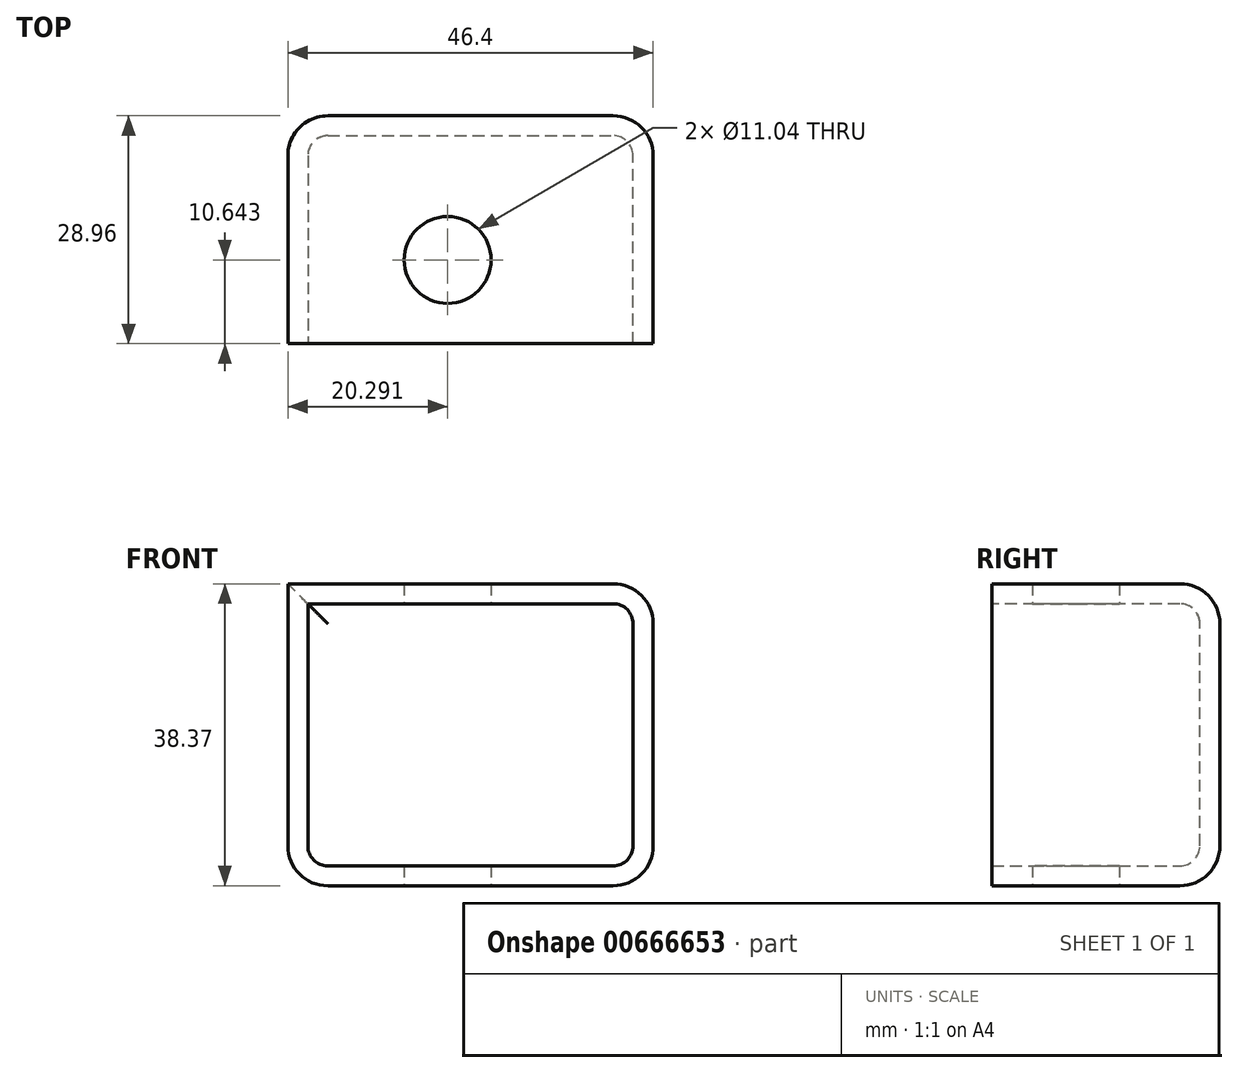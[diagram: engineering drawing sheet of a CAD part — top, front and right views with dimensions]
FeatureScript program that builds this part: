
annotation { "Feature Type Name" : "Feature", "Feature Type Description" : "" }
export const myFeature = defineFeature(function(context is Context, id is Id, definition is map)
    precondition{}
    {
        {
            var Q0;
            Q0=qCreatedBy(makeId("Front.planeOp"),FACE);
            var sketch = newSketch(context, id + "F0", { "sketchPlane" : qUnion([Q0])});
            skLineSegment(sketch, "E0.bottom", {"start": v(2.62, 0) * mm, "end": v(49.02, 0) * mm});
            skLineSegment(sketch, "E0.top", {"start": v(2.62, 38.37) * mm, "end": v(49.02, 38.37) * mm});
            skLineSegment(sketch, "E0.left", {"start": v(2.62, 0) * mm, "end": v(2.62, 38.37) * mm});
            skLineSegment(sketch, "E0.right", {"start": v(49.02, 0) * mm, "end": v(49.02, 38.37) * mm});
            skSolve(sketch);
        }
        {
            var Q0;
            Q0 = qSketchRegion(id + "F0", true);
            extrude(context, id + "F1", {"entities" : qUnion([Q0]), "endBound" : BoundingType.SYMMETRIC, "oppositeDirection" : true, "depth" : 28.96 * mm, "offsetDistance" : 25.4 * mm});
        }
        {
            var Q0;
            Q0=makeQuery(id+"F1.opExtrude","CAP_EDGE",EDGE,{"disambiguationData":[OSD([sQuery(id+"F0.wireOp",EDGE,"E0.right")])],"isStart":false});
            var Q1;
            Q1=makeQuery(id+"F1.opExtrude","SWEPT_EDGE",EDGE,{"disambiguationData":[OSD([sQuery(id+"F0.wireOp",EDGE,"E0.bottom"),sQuery(id+"F0.wireOp",EDGE,"E0.right")])]});
            var Q2;
            Q2=makeQuery(id+"F1.opExtrude","SWEPT_EDGE",EDGE,{"disambiguationData":[OSD([sQuery(id+"F0.wireOp",EDGE,"E0.bottom"),sQuery(id+"F0.wireOp",EDGE,"E0.left")])]});
            var Q3;
            Q3=makeQuery(id+"F1.opExtrude","CAP_EDGE",EDGE,{"disambiguationData":[OSD([sQuery(id+"F0.wireOp",EDGE,"E0.bottom")])],"isStart":false});
            var Q4;
            Q4=makeQuery(id+"F1.opExtrude","CAP_EDGE",EDGE,{"disambiguationData":[OSD([sQuery(id+"F0.wireOp",EDGE,"E0.left")])],"isStart":false});
            var Q5;
            Q5=makeQuery(id+"F1.opExtrude","CAP_EDGE",EDGE,{"disambiguationData":[OSD([sQuery(id+"F0.wireOp",EDGE,"E0.top")])],"isStart":false});
            var Q6;
            Q6=makeQuery(id+"F1.opExtrude","SWEPT_EDGE",EDGE,{"disambiguationData":[OSD([sQuery(id+"F0.wireOp",EDGE,"E0.top"),sQuery(id+"F0.wireOp",EDGE,"E0.right")])]});
            fillet(context, id + "F2", {"entities" : qUnion([Q0, Q1, Q2, Q3, Q4, Q5, Q6]), "radius" : 5.08 * mm, "tangentPropagation" : true, "allowEdgeOverflow" : false});
        }
        {
            var Q0;
            Q0=makeQuery(id+"F1.opExtrude","CAP_FACE",FACE,{"disambiguationData":[OSD([sQuery(id+"F0.wireOp",EDGE,"E0.bottom"),sQuery(id+"F0.wireOp",EDGE,"E0.top"),sQuery(id+"F0.wireOp",EDGE,"E0.left"),sQuery(id+"F0.wireOp",EDGE,"E0.right")])],"isStart":true});
            shell(context, id + "F3", {"entities" : qUnion([Q0]), "thickness" : 2.54 * mm});
        }
        {
            var Q0;
            Q0=makeQuery(id+"F1.opExtrude","SWEPT_FACE",FACE,{"disambiguationData":[OSD([sQuery(id+"F0.wireOp",EDGE,"E0.bottom")])]});
            var sketch = newSketch(context, id + "F4", { "sketchPlane" : qUnion([Q0])});
            skCircle(sketch, "E1", {"center": v(22.91, 3.84) * mm, "radius": 5.52 * mm});
            skSolve(sketch);
        }
        {
            var Q0;
            Q0 = qSketchRegion(id + "F4", true);
            extrude(context, id + "F5", {"entities" : qUnion([Q0]), "operationType" : NewBodyOperationType.REMOVE, "oppositeDirection" : true, "depth" : 38.86 * mm, "offsetDistance" : 25.4 * mm});
        }
    });
